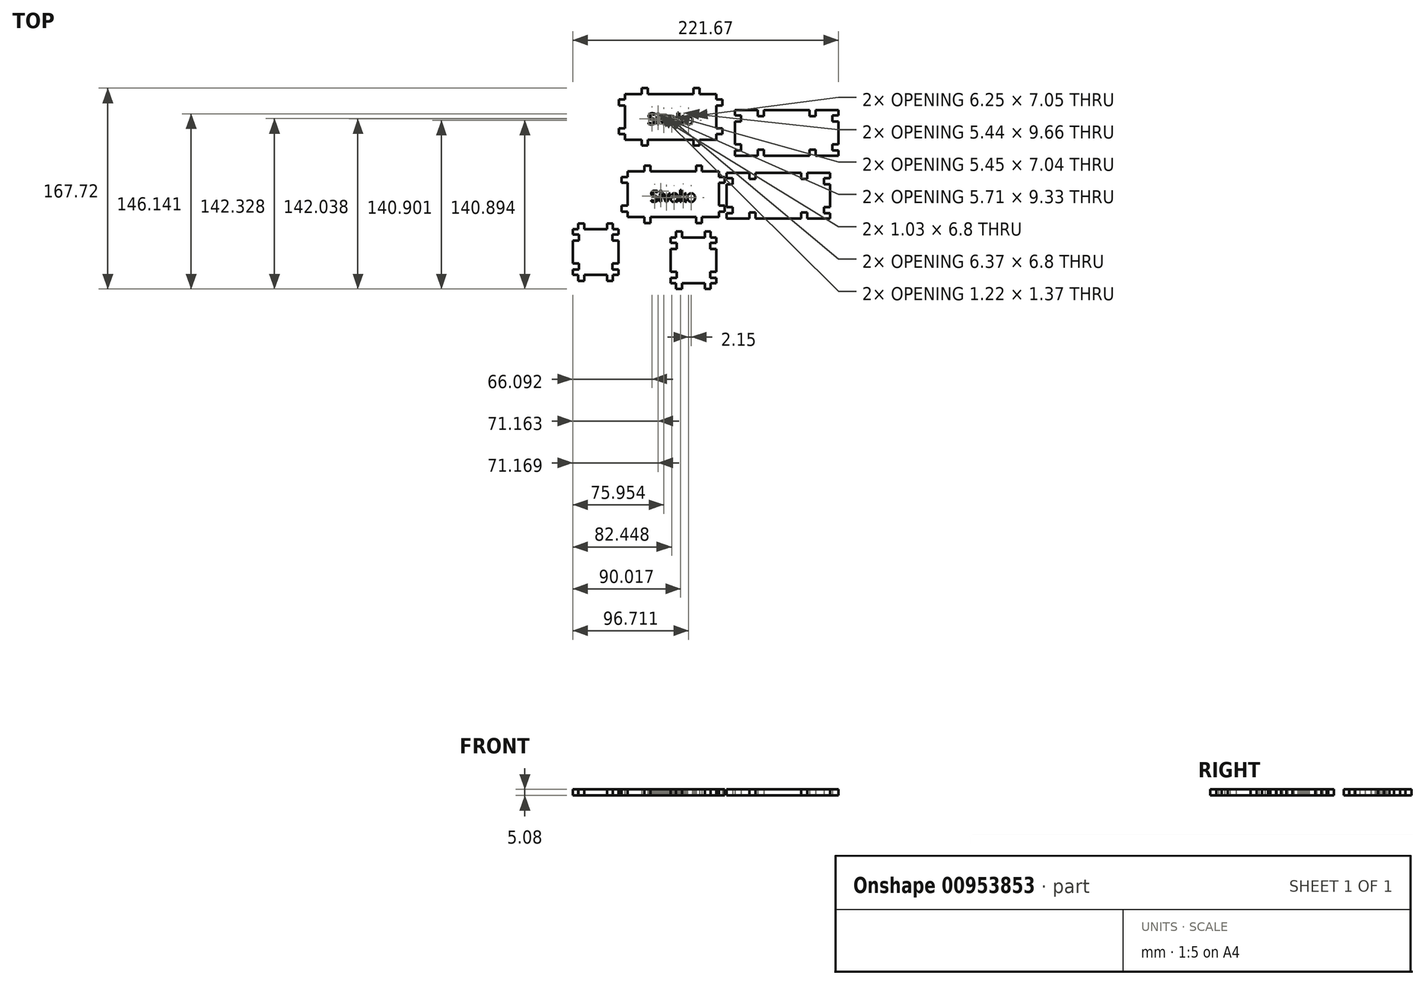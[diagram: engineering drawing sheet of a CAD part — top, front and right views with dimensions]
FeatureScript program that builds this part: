
annotation { "Feature Type Name" : "Feature", "Feature Type Description" : "" }
export const myFeature = defineFeature(function(context is Context, id is Id, definition is map)
    precondition{}
    {
        {
            var Q0;
            Q0=qCreatedBy(makeId("Top.planeOp"),FACE);
            var sketch = newSketch(context, id + "F0", { "sketchPlane" : qUnion([Q0])});
            skLineSegment(sketch, "E0.top", {"start": v(-38.1, -19.05) * mm, "end": v(38.1, -19.05) * mm});
            skLineSegment(sketch, "E0.right", {"start": v(38.1, 19.05) * mm, "end": v(38.1, -19.05) * mm});
            skPoint(sketch, "E0.middle", {"position": v(0, 0) * mm});
            skLineSegment(sketch, "E1", {"start": v(-38.1, 19.05) * mm, "end": v(-38.1, 0) * mm});
            skLineSegment(sketch, "E2", {"start": v(-38.1, 0) * mm, "end": v(-38.1, -19.05) * mm});
            skLineSegment(sketch, "E3", {"start": v(0, 0) * mm, "end": v(0, 19.05) * mm});
            skLineSegment(sketch, "E4", {"start": v(-38.1, 19.05) * mm, "end": v(0, 19.05) * mm});
            skLineSegment(sketch, "E5", {"start": v(0, 19.05) * mm, "end": v(38.1, 19.05) * mm});
            skLineSegment(sketch, "E6", {"start": v(-38.1, 0) * mm, "end": v(38.1, 0) * mm});
            skLineSegment(sketch, "E7", {"start": v(38.1, 14.61) * mm, "end": v(38.1, 14.61) * mm});
            skLineSegment(sketch, "E8", {"start": v(38.1, 9.52) * mm, "end": v(38.1, 9.52) * mm});
            skLineSegment(sketch, "E9.MirrorCS", {"start": v(38.1, -19.05) * mm, "end": v(38.1, 19.05) * mm});
            skLineSegment(sketch, "E10", {"start": v(38.1, -9.52) * mm, "end": v(38.1, -9.52) * mm});
            skLineSegment(sketch, "E11", {"start": v(38.1, -14.61) * mm, "end": v(38.1, -14.61) * mm});
            skLineSegment(sketch, "E12", {"start": v(-38.1, -14.61) * mm, "end": v(-38.1, -14.61) * mm});
            skLineSegment(sketch, "E13", {"start": v(-38.1, -9.52) * mm, "end": v(-38.1, -9.52) * mm});
            skLineSegment(sketch, "E14", {"start": v(-38.23, 9.65) * mm, "end": v(-38.23, 9.65) * mm});
            skLineSegment(sketch, "E15", {"start": v(-38.1, 9.53) * mm, "end": v(-43.05, 9.53) * mm});
            skLineSegment(sketch, "E16", {"start": v(-43.05, 9.53) * mm, "end": v(-43.05, 14.48) * mm});
            skLineSegment(sketch, "E17", {"start": v(-43.05, 14.48) * mm, "end": v(-38.1, 14.48) * mm});
            skLineSegment(sketch, "E18.MirrorCS", {"start": v(-38.1, -9.52) * mm, "end": v(-43.05, -9.52) * mm});
            skLineSegment(sketch, "E19.MirrorCS", {"start": v(-43.05, -9.52) * mm, "end": v(-43.05, -14.47) * mm});
            skLineSegment(sketch, "E20.MirrorCS", {"start": v(-43.05, -14.47) * mm, "end": v(-38.1, -14.47) * mm});
            skLineSegment(sketch, "E21", {"start": v(-38.1, -14.47) * mm, "end": v(-38.1, -14.47) * mm});
            skLineSegment(sketch, "E22.MirrorCS", {"start": v(43.05, 9.52) * mm, "end": v(43.05, 14.48) * mm});
            skLineSegment(sketch, "E23.MirrorCS", {"start": v(43.05, 14.48) * mm, "end": v(38.1, 14.48) * mm});
            skLineSegment(sketch, "E24.MirrorCS", {"start": v(38.1, 9.52) * mm, "end": v(43.05, 9.52) * mm});
            skLineSegment(sketch, "E25.MirrorCS", {"start": v(38.1, -9.52) * mm, "end": v(43.05, -9.52) * mm});
            skLineSegment(sketch, "E26.MirrorCS", {"start": v(43.05, -14.48) * mm, "end": v(38.1, -14.48) * mm});
            skLineSegment(sketch, "E27.MirrorCS", {"start": v(43.05, -9.52) * mm, "end": v(43.05, -14.48) * mm});
            skLineSegment(sketch, "E28", {"start": v(-19.05, 19.05) * mm, "end": v(-19.05, 24) * mm});
            skLineSegment(sketch, "E29", {"start": v(-19.05, 24) * mm, "end": v(-24, 24) * mm});
            skLineSegment(sketch, "E30", {"start": v(-24, 24) * mm, "end": v(-24, 19.05) * mm});
            skLineSegment(sketch, "E31.MirrorCS", {"start": v(19.05, 19.05) * mm, "end": v(19.05, 24) * mm});
            skLineSegment(sketch, "E32.MirrorCS", {"start": v(19.05, 24) * mm, "end": v(24, 24) * mm});
            skLineSegment(sketch, "E33.MirrorCS", {"start": v(24, 24) * mm, "end": v(24, 19.05) * mm});
            skLineSegment(sketch, "E34.MirrorCS", {"start": v(-19.05, -19.05) * mm, "end": v(-19.05, -24) * mm});
            skLineSegment(sketch, "E35.MirrorCS", {"start": v(-24, -24) * mm, "end": v(-24, -19.05) * mm});
            skLineSegment(sketch, "E36.MirrorCS", {"start": v(-19.05, -24) * mm, "end": v(-24, -24) * mm});
            skLineSegment(sketch, "E37.MirrorCS", {"start": v(19.05, -19.05) * mm, "end": v(19.05, -24) * mm});
            skLineSegment(sketch, "E38.MirrorCS", {"start": v(19.05, -24) * mm, "end": v(24, -24) * mm});
            skLineSegment(sketch, "E39.MirrorCS", {"start": v(24, -24) * mm, "end": v(24, -19.05) * mm});
            skLineSegment(sketch, "E40", {"start": v(0, 9.52) * mm, "end": v(-38.1, 9.53) * mm});
            skLineSegment(sketch, "E41", {"start": v(0, 0) * mm, "end": v(0, -19.05) * mm});
            skLineSegment(sketch, "E42", {"start": v(0, -9.52) * mm, "end": v(38.1, -9.52) * mm});
            skText(sketch, "E43", { "text": "Sivako", "fontName": "OpenSans-Regular.ttf"});
            skPoint(sketch, "E43.firstSnap0", {"position": v(-19.05, 9.53) * mm});
            skPoint(sketch, "E43.secondSnap0", {"position": v(19.05, -9.52) * mm});
            skLineSegment(sketch, "E44.top", {"start": v(-40.26, 45.52) * mm, "end": v(35.94, 45.52) * mm});
            skLineSegment(sketch, "E44.right", {"start": v(35.95, 83.62) * mm, "end": v(35.94, 45.52) * mm});
            skPoint(sketch, "E44.middle", {"position": v(-2.16, 64.57) * mm});
            skLineSegment(sketch, "E45", {"start": v(-40.25, 83.62) * mm, "end": v(-40.26, 64.57) * mm});
            skLineSegment(sketch, "E46", {"start": v(-40.26, 64.57) * mm, "end": v(-40.26, 45.52) * mm});
            skLineSegment(sketch, "E47", {"start": v(-2.16, 64.57) * mm, "end": v(-2.15, 83.62) * mm});
            skLineSegment(sketch, "E48", {"start": v(-40.25, 83.62) * mm, "end": v(-2.15, 83.62) * mm});
            skLineSegment(sketch, "E49", {"start": v(-2.15, 83.62) * mm, "end": v(35.95, 83.62) * mm});
            skLineSegment(sketch, "E50", {"start": v(-40.26, 64.57) * mm, "end": v(35.94, 64.57) * mm});
            skLineSegment(sketch, "E51", {"start": v(35.95, 79.18) * mm, "end": v(35.94, 79.18) * mm});
            skLineSegment(sketch, "E52", {"start": v(35.95, 74.1) * mm, "end": v(35.94, 74.1) * mm});
            skLineSegment(sketch, "E53.MirrorCS", {"start": v(35.94, 45.52) * mm, "end": v(35.95, 83.62) * mm});
            skLineSegment(sketch, "E54", {"start": v(35.94, 55.04) * mm, "end": v(35.94, 55.04) * mm});
            skLineSegment(sketch, "E55", {"start": v(35.94, 49.95) * mm, "end": v(35.94, 49.95) * mm});
            skLineSegment(sketch, "E56", {"start": v(-40.26, 49.96) * mm, "end": v(-40.26, 49.96) * mm});
            skLineSegment(sketch, "E57", {"start": v(-40.26, 55.05) * mm, "end": v(-40.26, 55.05) * mm});
            skLineSegment(sketch, "E58", {"start": v(-40.38, 74.22) * mm, "end": v(-40.38, 74.22) * mm});
            skLineSegment(sketch, "E59", {"start": v(-40.26, 74.1) * mm, "end": v(-45.2, 74.1) * mm});
            skLineSegment(sketch, "E60", {"start": v(-45.2, 74.1) * mm, "end": v(-45.2, 79.05) * mm});
            skLineSegment(sketch, "E61", {"start": v(-45.2, 79.05) * mm, "end": v(-40.26, 79.05) * mm});
            skLineSegment(sketch, "E62.MirrorCS", {"start": v(-40.26, 55.05) * mm, "end": v(-45.2, 55.05) * mm});
            skLineSegment(sketch, "E63.MirrorCS", {"start": v(-45.2, 55.05) * mm, "end": v(-45.2, 50.1) * mm});
            skLineSegment(sketch, "E64.MirrorCS", {"start": v(-45.2, 50.1) * mm, "end": v(-40.26, 50.1) * mm});
            skLineSegment(sketch, "E65", {"start": v(-40.26, 50.1) * mm, "end": v(-40.26, 50.1) * mm});
            skLineSegment(sketch, "E66", {"start": v(-40.26, 55.05) * mm, "end": v(-40.25, 55.05) * mm});
            skLineSegment(sketch, "E67.MirrorCS", {"start": v(40.9, 74.1) * mm, "end": v(40.9, 79.04) * mm});
            skLineSegment(sketch, "E68.MirrorCS", {"start": v(40.9, 79.04) * mm, "end": v(35.95, 79.04) * mm});
            skLineSegment(sketch, "E69.MirrorCS", {"start": v(35.95, 74.1) * mm, "end": v(40.9, 74.1) * mm});
            skLineSegment(sketch, "E70.MirrorCS", {"start": v(35.94, 55.04) * mm, "end": v(40.9, 55.04) * mm});
            skLineSegment(sketch, "E71.MirrorCS", {"start": v(40.9, 50.1) * mm, "end": v(35.94, 50.1) * mm});
            skLineSegment(sketch, "E72.MirrorCS", {"start": v(40.9, 55.04) * mm, "end": v(40.9, 50.1) * mm});
            skLineSegment(sketch, "E73", {"start": v(-21.2, 83.62) * mm, "end": v(-21.2, 88.57) * mm});
            skLineSegment(sketch, "E74", {"start": v(-21.2, 88.57) * mm, "end": v(-26.16, 88.57) * mm});
            skLineSegment(sketch, "E75", {"start": v(-26.16, 88.57) * mm, "end": v(-26.16, 83.62) * mm});
            skLineSegment(sketch, "E76.MirrorCS", {"start": v(16.9, 83.62) * mm, "end": v(16.9, 88.57) * mm});
            skLineSegment(sketch, "E77.MirrorCS", {"start": v(16.9, 88.57) * mm, "end": v(21.85, 88.57) * mm});
            skLineSegment(sketch, "E78.MirrorCS", {"start": v(21.85, 88.57) * mm, "end": v(21.85, 83.62) * mm});
            skLineSegment(sketch, "E79.MirrorCS", {"start": v(-21.2, 45.52) * mm, "end": v(-21.2, 40.57) * mm});
            skLineSegment(sketch, "E80.MirrorCS", {"start": v(-26.16, 40.57) * mm, "end": v(-26.16, 45.52) * mm});
            skLineSegment(sketch, "E81.MirrorCS", {"start": v(-21.2, 40.57) * mm, "end": v(-26.16, 40.57) * mm});
            skLineSegment(sketch, "E82.MirrorCS", {"start": v(16.9, 45.52) * mm, "end": v(16.9, 40.57) * mm});
            skLineSegment(sketch, "E83.MirrorCS", {"start": v(16.9, 40.57) * mm, "end": v(21.85, 40.57) * mm});
            skLineSegment(sketch, "E84.MirrorCS", {"start": v(21.85, 40.57) * mm, "end": v(21.85, 45.52) * mm});
            skLineSegment(sketch, "E85", {"start": v(-2.15, 74.1) * mm, "end": v(-40.26, 74.1) * mm});
            skLineSegment(sketch, "E86", {"start": v(-2.16, 64.57) * mm, "end": v(-2.16, 45.52) * mm});
            skLineSegment(sketch, "E87", {"start": v(-2.16, 55.04) * mm, "end": v(35.94, 55.04) * mm});
            skText(sketch, "E88", { "text": "Sivako", "fontName": "OpenSans-Regular.ttf"});
            skPoint(sketch, "E88.firstSnap0", {"position": v(-21.2, 74.1) * mm});
            skPoint(sketch, "E88.secondSnap0", {"position": v(16.9, 55.04) * mm});
            const initialGuessF0  = {"E43": [-0.01905, -0.00622, 1, 0, 0.00915], "E88": [-0.0212, 0.05835, 1, 0, 0.00915]};
            skSetInitialGuess(sketch, initialGuessF0);
            skSolve(sketch);
        }
        {
            var Q0;
            Q0 = qSketchRegion(id + "F0", true);
            var Q1;
            {var subQ6=sQuery(id+"F0.wireOp",EDGE,"E0.top");Q1=makeQuery(id+"F0.imprint","IMPRINT",FACE,{"disambiguationData":[TD([[makeQuery(id+"F0.imprint","IMPRINT",EDGE,{"derivedFrom":subQ6}),1.0]])]});}
            var Q2;
            {var subQ0=sQuery(id+"F0.wireOp",EDGE,"E43.sketch_text.stroke-40");Q2=makeQuery(id+"F0.imprint","IMPRINT",FACE,{"disambiguationData":[TD([[makeQuery(id+"F0.imprint","IMPRINT",EDGE,{"derivedFrom":subQ0}),1.0]])]});}
            var Q3;
            {var subQ0=sQuery(id+"F0.wireOp",EDGE,"E43.sketch_text.stroke-54");Q3=makeQuery(id+"F0.imprint","IMPRINT",FACE,{"disambiguationData":[TD([[makeQuery(id+"F0.imprint","IMPRINT",EDGE,{"derivedFrom":subQ0}),1.0]])]});}
            extrude(context, id + "F1", {"entities" : qUnion([Q0, Q1, Q2, Q3]), "depth" : 5.08 * mm, "offsetDistance" : 25.4 * mm});
        }
        {
            var Q0;
            Q0=qCreatedBy(makeId("Top.planeOp"),FACE);
            var sketch = newSketch(context, id + "F2", { "sketchPlane" : qUnion([Q0])});
            skLineSegment(sketch, "E89.top", {"start": v(-83.78, -67.33) * mm, "end": v(-45.68, -67.33) * mm});
            skLineSegment(sketch, "E89.right", {"start": v(-45.68, -29.23) * mm, "end": v(-45.68, -67.33) * mm});
            skPoint(sketch, "E89.middle", {"position": v(-64.73, -48.28) * mm});
            skLineSegment(sketch, "E90", {"start": v(-83.78, -48.28) * mm, "end": v(-45.68, -48.28) * mm});
            skLineSegment(sketch, "E91", {"start": v(-64.73, -29.23) * mm, "end": v(-64.73, -67.33) * mm});
            skLineSegment(sketch, "E92", {"start": v(-83.78, -29.23) * mm, "end": v(-83.78, -48.28) * mm});
            skLineSegment(sketch, "E93", {"start": v(-83.78, -48.28) * mm, "end": v(-83.78, -67.33) * mm});
            skLineSegment(sketch, "E94", {"start": v(-83.78, -38.75) * mm, "end": v(-78.7, -38.75) * mm});
            skLineSegment(sketch, "E95", {"start": v(-78.7, -38.75) * mm, "end": v(-78.7, -33.67) * mm});
            skLineSegment(sketch, "E96", {"start": v(-78.7, -33.67) * mm, "end": v(-83.78, -33.67) * mm});
            skLineSegment(sketch, "E97.MirrorCS", {"start": v(-83.78, -57.8) * mm, "end": v(-78.7, -57.8) * mm});
            skLineSegment(sketch, "E98.MirrorCS", {"start": v(-78.7, -57.8) * mm, "end": v(-78.7, -62.88) * mm});
            skLineSegment(sketch, "E99.MirrorCS", {"start": v(-78.7, -62.88) * mm, "end": v(-83.78, -62.88) * mm});
            skLineSegment(sketch, "E100.MirrorCS", {"start": v(-50.76, -38.75) * mm, "end": v(-50.76, -33.67) * mm});
            skLineSegment(sketch, "E101.MirrorCS", {"start": v(-50.76, -33.67) * mm, "end": v(-45.68, -33.67) * mm});
            skLineSegment(sketch, "E102.MirrorCS", {"start": v(-45.68, -38.75) * mm, "end": v(-50.76, -38.75) * mm});
            skLineSegment(sketch, "E103.MirrorCS", {"start": v(-45.68, -57.8) * mm, "end": v(-50.76, -57.8) * mm});
            skLineSegment(sketch, "E104.MirrorCS", {"start": v(-50.76, -57.8) * mm, "end": v(-50.76, -62.88) * mm});
            skLineSegment(sketch, "E105.MirrorCS", {"start": v(-50.76, -62.88) * mm, "end": v(-45.68, -62.88) * mm});
            skLineSegment(sketch, "E106", {"start": v(-83.78, -29.23) * mm, "end": v(-64.73, -29.23) * mm});
            skLineSegment(sketch, "E107", {"start": v(-64.73, -29.23) * mm, "end": v(-45.68, -29.23) * mm});
            skLineSegment(sketch, "E108", {"start": v(-74.25, -29.23) * mm, "end": v(-74.25, -24.28) * mm});
            skLineSegment(sketch, "E109", {"start": v(-74.25, -24.28) * mm, "end": v(-79.2, -24.28) * mm});
            skLineSegment(sketch, "E110", {"start": v(-79.2, -24.28) * mm, "end": v(-79.2, -29.23) * mm});
            skLineSegment(sketch, "E111", {"start": v(-55.2, -29.23) * mm, "end": v(-55.2, -24.28) * mm});
            skLineSegment(sketch, "E112", {"start": v(-55.2, -24.28) * mm, "end": v(-50.25, -24.28) * mm});
            skLineSegment(sketch, "E113", {"start": v(-50.25, -24.28) * mm, "end": v(-50.25, -29.23) * mm});
            skLineSegment(sketch, "E114.MirrorCS", {"start": v(-74.25, -67.33) * mm, "end": v(-74.25, -72.28) * mm});
            skLineSegment(sketch, "E115.MirrorCS", {"start": v(-74.25, -72.28) * mm, "end": v(-79.2, -72.28) * mm});
            skLineSegment(sketch, "E116.MirrorCS", {"start": v(-79.2, -72.28) * mm, "end": v(-79.2, -67.33) * mm});
            skLineSegment(sketch, "E117.MirrorCS", {"start": v(-55.2, -67.33) * mm, "end": v(-55.2, -72.28) * mm});
            skLineSegment(sketch, "E118.MirrorCS", {"start": v(-55.2, -72.28) * mm, "end": v(-50.25, -72.28) * mm});
            skLineSegment(sketch, "E119.MirrorCS", {"start": v(-50.25, -72.28) * mm, "end": v(-50.25, -67.33) * mm});
            skLineSegment(sketch, "E120.top", {"start": v(-2.2, -74.2) * mm, "end": v(35.9, -74.2) * mm});
            skLineSegment(sketch, "E120.right", {"start": v(35.9, -36.1) * mm, "end": v(35.9, -74.2) * mm});
            skPoint(sketch, "E120.middle", {"position": v(16.85, -55.15) * mm});
            skLineSegment(sketch, "E121", {"start": v(-2.2, -55.15) * mm, "end": v(35.9, -55.15) * mm});
            skLineSegment(sketch, "E122", {"start": v(16.85, -36.1) * mm, "end": v(16.85, -74.2) * mm});
            skLineSegment(sketch, "E123", {"start": v(-2.2, -36.1) * mm, "end": v(-2.2, -55.15) * mm});
            skLineSegment(sketch, "E124", {"start": v(-2.2, -55.15) * mm, "end": v(-2.2, -74.2) * mm});
            skLineSegment(sketch, "E125", {"start": v(-2.2, -45.62) * mm, "end": v(2.88, -45.62) * mm});
            skLineSegment(sketch, "E126", {"start": v(2.88, -45.62) * mm, "end": v(2.88, -40.54) * mm});
            skLineSegment(sketch, "E127", {"start": v(2.88, -40.54) * mm, "end": v(-2.2, -40.54) * mm});
            skLineSegment(sketch, "E128.MirrorCS", {"start": v(-2.2, -64.67) * mm, "end": v(2.88, -64.67) * mm});
            skLineSegment(sketch, "E129.MirrorCS", {"start": v(2.88, -64.67) * mm, "end": v(2.88, -69.75) * mm});
            skLineSegment(sketch, "E130.MirrorCS", {"start": v(2.88, -69.75) * mm, "end": v(-2.2, -69.75) * mm});
            skLineSegment(sketch, "E131.MirrorCS", {"start": v(30.82, -45.62) * mm, "end": v(30.82, -40.54) * mm});
            skLineSegment(sketch, "E132.MirrorCS", {"start": v(30.82, -40.54) * mm, "end": v(35.9, -40.54) * mm});
            skLineSegment(sketch, "E133.MirrorCS", {"start": v(35.9, -45.62) * mm, "end": v(30.82, -45.62) * mm});
            skLineSegment(sketch, "E134.MirrorCS", {"start": v(35.9, -64.67) * mm, "end": v(30.82, -64.67) * mm});
            skLineSegment(sketch, "E135.MirrorCS", {"start": v(30.82, -64.67) * mm, "end": v(30.82, -69.75) * mm});
            skLineSegment(sketch, "E136.MirrorCS", {"start": v(30.82, -69.75) * mm, "end": v(35.9, -69.75) * mm});
            skLineSegment(sketch, "E137", {"start": v(-2.2, -36.1) * mm, "end": v(16.85, -36.1) * mm});
            skLineSegment(sketch, "E138", {"start": v(16.85, -36.1) * mm, "end": v(35.9, -36.1) * mm});
            skLineSegment(sketch, "E139", {"start": v(7.33, -36.1) * mm, "end": v(7.33, -31.14) * mm});
            skLineSegment(sketch, "E140", {"start": v(7.33, -31.14) * mm, "end": v(2.37, -31.14) * mm});
            skLineSegment(sketch, "E141", {"start": v(2.37, -31.14) * mm, "end": v(2.37, -36.1) * mm});
            skLineSegment(sketch, "E142", {"start": v(26.38, -36.1) * mm, "end": v(26.38, -31.14) * mm});
            skLineSegment(sketch, "E143", {"start": v(26.38, -31.14) * mm, "end": v(31.33, -31.14) * mm});
            skLineSegment(sketch, "E144", {"start": v(31.33, -31.14) * mm, "end": v(31.33, -36.1) * mm});
            skLineSegment(sketch, "E145.MirrorCS", {"start": v(7.33, -74.2) * mm, "end": v(7.33, -79.15) * mm});
            skLineSegment(sketch, "E146.MirrorCS", {"start": v(7.33, -79.15) * mm, "end": v(2.37, -79.15) * mm});
            skLineSegment(sketch, "E147.MirrorCS", {"start": v(2.37, -79.15) * mm, "end": v(2.37, -74.2) * mm});
            skLineSegment(sketch, "E148.MirrorCS", {"start": v(26.38, -74.2) * mm, "end": v(26.38, -79.15) * mm});
            skLineSegment(sketch, "E149.MirrorCS", {"start": v(26.38, -79.15) * mm, "end": v(31.33, -79.15) * mm});
            skLineSegment(sketch, "E150.MirrorCS", {"start": v(31.33, -79.15) * mm, "end": v(31.33, -74.2) * mm});
            skLineSegment(sketch, "E151.top", {"start": v(44.41, -20.23) * mm, "end": v(130.77, -20.23) * mm});
            skLineSegment(sketch, "E151.right", {"start": v(130.77, 17.87) * mm, "end": v(130.77, -20.23) * mm});
            skPoint(sketch, "E151.middle", {"position": v(87.6, -1.18) * mm});
            skLineSegment(sketch, "E152", {"start": v(44.41, 17.87) * mm, "end": v(44.41, -1.18) * mm});
            skLineSegment(sketch, "E153", {"start": v(44.41, -1.18) * mm, "end": v(44.41, -20.23) * mm});
            skLineSegment(sketch, "E154", {"start": v(44.41, 17.87) * mm, "end": v(87.6, 17.87) * mm});
            skLineSegment(sketch, "E155", {"start": v(87.6, 17.87) * mm, "end": v(130.77, 17.87) * mm});
            skLineSegment(sketch, "E156", {"start": v(87.6, 17.87) * mm, "end": v(49.5, 17.87) * mm});
            skLineSegment(sketch, "E157", {"start": v(87.6, 17.87) * mm, "end": v(125.7, 17.87) * mm});
            skLineSegment(sketch, "E158", {"start": v(68.54, 17.87) * mm, "end": v(68.54, 12.8) * mm});
            skLineSegment(sketch, "E159", {"start": v(68.54, 12.8) * mm, "end": v(63.46, 12.8) * mm});
            skLineSegment(sketch, "E160", {"start": v(63.46, 12.8) * mm, "end": v(63.46, 17.87) * mm});
            skLineSegment(sketch, "E161.MirrorCS", {"start": v(106.64, 17.87) * mm, "end": v(106.64, 12.8) * mm});
            skLineSegment(sketch, "E162.MirrorCS", {"start": v(106.64, 12.8) * mm, "end": v(111.72, 12.8) * mm});
            skLineSegment(sketch, "E163.MirrorCS", {"start": v(111.72, 12.8) * mm, "end": v(111.72, 17.87) * mm});
            skLineSegment(sketch, "E164.MirrorCS", {"start": v(68.54, -15.15) * mm, "end": v(63.46, -15.15) * mm});
            skLineSegment(sketch, "E165.MirrorCS", {"start": v(63.46, -15.15) * mm, "end": v(63.46, -20.23) * mm});
            skLineSegment(sketch, "E166.MirrorCS", {"start": v(68.54, -20.23) * mm, "end": v(68.54, -15.15) * mm});
            skLineSegment(sketch, "E167.MirrorCS", {"start": v(106.64, -15.15) * mm, "end": v(111.72, -15.15) * mm});
            skLineSegment(sketch, "E168.MirrorCS", {"start": v(106.64, -20.23) * mm, "end": v(106.64, -15.15) * mm});
            skLineSegment(sketch, "E169.MirrorCS", {"start": v(111.72, -15.15) * mm, "end": v(111.72, -20.23) * mm});
            skLineSegment(sketch, "E170.MirrorCS", {"start": v(49.5, 13.43) * mm, "end": v(44.41, 13.43) * mm});
            skLineSegment(sketch, "E171.MirrorCS", {"start": v(49.5, 8.35) * mm, "end": v(49.5, 13.43) * mm});
            skLineSegment(sketch, "E172.MirrorCS", {"start": v(44.41, 8.35) * mm, "end": v(49.5, 8.35) * mm});
            skLineSegment(sketch, "E173.MirrorCS", {"start": v(49.5, -10.7) * mm, "end": v(49.5, -15.78) * mm});
            skLineSegment(sketch, "E174.MirrorCS", {"start": v(49.5, -15.78) * mm, "end": v(44.41, -15.78) * mm});
            skLineSegment(sketch, "E175.MirrorCS", {"start": v(44.41, -10.7) * mm, "end": v(49.5, -10.7) * mm});
            skLineSegment(sketch, "E176.MirrorCS", {"start": v(125.7, 8.35) * mm, "end": v(125.7, 13.43) * mm});
            skLineSegment(sketch, "E177.MirrorCS", {"start": v(125.7, 13.43) * mm, "end": v(130.77, 13.43) * mm});
            skLineSegment(sketch, "E178.MirrorCS", {"start": v(130.77, 8.35) * mm, "end": v(125.7, 8.35) * mm});
            skLineSegment(sketch, "E179.MirrorCS", {"start": v(130.77, -10.7) * mm, "end": v(125.7, -10.7) * mm});
            skLineSegment(sketch, "E180.MirrorCS", {"start": v(125.7, -10.7) * mm, "end": v(125.7, -15.78) * mm});
            skLineSegment(sketch, "E181.MirrorCS", {"start": v(125.7, -15.78) * mm, "end": v(130.77, -15.78) * mm});
            skLineSegment(sketch, "E182.top", {"start": v(51.53, 32.1) * mm, "end": v(137.89, 32.1) * mm});
            skLineSegment(sketch, "E182.right", {"start": v(137.89, 70.2) * mm, "end": v(137.89, 32.1) * mm});
            skPoint(sketch, "E182.middle", {"position": v(94.7, 51.15) * mm});
            skLineSegment(sketch, "E183", {"start": v(51.53, 51.15) * mm, "end": v(137.89, 51.15) * mm});
            skLineSegment(sketch, "E184", {"start": v(51.53, 70.2) * mm, "end": v(51.53, 51.15) * mm});
            skLineSegment(sketch, "E185", {"start": v(51.53, 51.15) * mm, "end": v(51.53, 32.1) * mm});
            skLineSegment(sketch, "E186", {"start": v(94.7, 51.15) * mm, "end": v(94.7, 70.2) * mm});
            skLineSegment(sketch, "E187", {"start": v(51.53, 70.2) * mm, "end": v(94.7, 70.2) * mm});
            skLineSegment(sketch, "E188", {"start": v(94.7, 70.2) * mm, "end": v(137.89, 70.2) * mm});
            skLineSegment(sketch, "E189", {"start": v(94.7, 70.2) * mm, "end": v(56.6, 70.2) * mm});
            skLineSegment(sketch, "E190", {"start": v(94.7, 70.2) * mm, "end": v(132.8, 70.2) * mm});
            skLineSegment(sketch, "E191", {"start": v(75.66, 70.2) * mm, "end": v(75.66, 65.12) * mm});
            skLineSegment(sketch, "E192", {"start": v(75.66, 65.12) * mm, "end": v(70.58, 65.12) * mm});
            skLineSegment(sketch, "E193", {"start": v(70.58, 65.12) * mm, "end": v(70.58, 70.2) * mm});
            skLineSegment(sketch, "E194.MirrorCS", {"start": v(113.76, 70.2) * mm, "end": v(113.76, 65.12) * mm});
            skLineSegment(sketch, "E195.MirrorCS", {"start": v(113.76, 65.12) * mm, "end": v(118.84, 65.12) * mm});
            skLineSegment(sketch, "E196.MirrorCS", {"start": v(118.84, 65.12) * mm, "end": v(118.84, 70.2) * mm});
            skLineSegment(sketch, "E197.MirrorCS", {"start": v(75.66, 37.18) * mm, "end": v(70.58, 37.18) * mm});
            skLineSegment(sketch, "E198.MirrorCS", {"start": v(70.58, 37.18) * mm, "end": v(70.58, 32.1) * mm});
            skLineSegment(sketch, "E199.MirrorCS", {"start": v(75.66, 32.1) * mm, "end": v(75.66, 37.18) * mm});
            skLineSegment(sketch, "E200.MirrorCS", {"start": v(113.76, 37.18) * mm, "end": v(118.84, 37.18) * mm});
            skLineSegment(sketch, "E201.MirrorCS", {"start": v(113.76, 32.1) * mm, "end": v(113.76, 37.18) * mm});
            skLineSegment(sketch, "E202.MirrorCS", {"start": v(118.84, 37.18) * mm, "end": v(118.84, 32.1) * mm});
            skLineSegment(sketch, "E203.MirrorCS", {"start": v(56.6, 65.76) * mm, "end": v(51.53, 65.76) * mm});
            skLineSegment(sketch, "E204.MirrorCS", {"start": v(56.6, 60.68) * mm, "end": v(56.6, 65.76) * mm});
            skLineSegment(sketch, "E205.MirrorCS", {"start": v(51.53, 60.68) * mm, "end": v(56.6, 60.68) * mm});
            skLineSegment(sketch, "E206.MirrorCS", {"start": v(56.6, 41.63) * mm, "end": v(56.6, 36.55) * mm});
            skLineSegment(sketch, "E207.MirrorCS", {"start": v(56.6, 36.55) * mm, "end": v(51.53, 36.55) * mm});
            skLineSegment(sketch, "E208.MirrorCS", {"start": v(51.53, 41.63) * mm, "end": v(56.6, 41.63) * mm});
            skLineSegment(sketch, "E209.MirrorCS", {"start": v(132.8, 60.68) * mm, "end": v(132.8, 65.76) * mm});
            skLineSegment(sketch, "E210.MirrorCS", {"start": v(132.8, 65.76) * mm, "end": v(137.89, 65.76) * mm});
            skLineSegment(sketch, "E211.MirrorCS", {"start": v(137.89, 60.68) * mm, "end": v(132.8, 60.68) * mm});
            skLineSegment(sketch, "E212.MirrorCS", {"start": v(137.89, 41.63) * mm, "end": v(132.8, 41.63) * mm});
            skLineSegment(sketch, "E213.MirrorCS", {"start": v(132.8, 41.63) * mm, "end": v(132.8, 36.55) * mm});
            skLineSegment(sketch, "E214.MirrorCS", {"start": v(132.8, 36.55) * mm, "end": v(137.89, 36.55) * mm});
            skPoint(sketch, "E215.orphan", {"position": v(130.77, -1.18) * mm});
            skSolve(sketch);
        }
        {
            var Q0;
            {var subQ0=sQuery(id+"F2.wireOp",EDGE,"E94");Q0=makeQuery(id+"F2.imprint","IMPRINT",FACE,{"disambiguationData":[TD([[makeQuery(id+"F2.imprint","IMPRINT",EDGE,{"derivedFrom":subQ0}),-1.0]])]});}
            var Q1;
            {var subQ10=sQuery(id+"F2.wireOp",EDGE,"E97.MirrorCS");Q1=makeQuery(id+"F2.imprint","IMPRINT",FACE,{"disambiguationData":[TD([[makeQuery(id+"F2.imprint","IMPRINT",EDGE,{"derivedFrom":subQ10}),1.0]])]});}
            var Q2;
            {var subQ3=sQuery(id+"F2.wireOp",EDGE,"E103.MirrorCS");Q2=makeQuery(id+"F2.imprint","IMPRINT",FACE,{"disambiguationData":[TD([[makeQuery(id+"F2.imprint","IMPRINT",EDGE,{"derivedFrom":subQ3}),-1.0]])]});}
            var Q3;
            Q3=makeQuery(id+"F2.imprint","IMPRINT",FACE,{"disambiguationData":[TD([[makeQuery(id+"F2.imprint","IMPRINT",EDGE,{"derivedFrom":sQuery(id+"F2.wireOp",EDGE,"E100.MirrorCS")}),1.0]])]});
            var Q4;
            {var subQ0=sQuery(id+"F2.wireOp",EDGE,"E117.MirrorCS");Q4=makeQuery(id+"F2.imprint","IMPRINT",FACE,{"disambiguationData":[TD([[makeQuery(id+"F2.imprint","IMPRINT",EDGE,{"derivedFrom":subQ0}),1.0]])]});}
            var Q5;
            {var subQ0=sQuery(id+"F2.wireOp",EDGE,"E114.MirrorCS");Q5=makeQuery(id+"F2.imprint","IMPRINT",FACE,{"disambiguationData":[TD([[makeQuery(id+"F2.imprint","IMPRINT",EDGE,{"derivedFrom":subQ0}),-1.0]])]});}
            var Q6;
            {var subQ0=sQuery(id+"F2.wireOp",EDGE,"E108");Q6=makeQuery(id+"F2.imprint","IMPRINT",FACE,{"disambiguationData":[TD([[makeQuery(id+"F2.imprint","IMPRINT",EDGE,{"derivedFrom":subQ0}),1.0]])]});}
            var Q7;
            {var subQ0=sQuery(id+"F2.wireOp",EDGE,"E111");Q7=makeQuery(id+"F2.imprint","IMPRINT",FACE,{"disambiguationData":[TD([[makeQuery(id+"F2.imprint","IMPRINT",EDGE,{"derivedFrom":subQ0}),-1.0]])]});}
            var Q8;
            {var subQ10=sQuery(id+"F2.wireOp",EDGE,"E128.MirrorCS");Q8=makeQuery(id+"F2.imprint","IMPRINT",FACE,{"disambiguationData":[TD([[makeQuery(id+"F2.imprint","IMPRINT",EDGE,{"derivedFrom":subQ10}),1.0]])]});}
            var Q9;
            {var subQ3=sQuery(id+"F2.wireOp",EDGE,"E134.MirrorCS");Q9=makeQuery(id+"F2.imprint","IMPRINT",FACE,{"disambiguationData":[TD([[makeQuery(id+"F2.imprint","IMPRINT",EDGE,{"derivedFrom":subQ3}),-1.0]])]});}
            var Q10;
            Q10=makeQuery(id+"F2.imprint","IMPRINT",FACE,{"disambiguationData":[TD([[makeQuery(id+"F2.imprint","IMPRINT",EDGE,{"derivedFrom":sQuery(id+"F2.wireOp",EDGE,"E131.MirrorCS")}),1.0]])]});
            var Q11;
            {var subQ0=sQuery(id+"F2.wireOp",EDGE,"E125");Q11=makeQuery(id+"F2.imprint","IMPRINT",FACE,{"disambiguationData":[TD([[makeQuery(id+"F2.imprint","IMPRINT",EDGE,{"derivedFrom":subQ0}),-1.0]])]});}
            var Q12;
            {var subQ0=sQuery(id+"F2.wireOp",EDGE,"E148.MirrorCS");Q12=makeQuery(id+"F2.imprint","IMPRINT",FACE,{"disambiguationData":[TD([[makeQuery(id+"F2.imprint","IMPRINT",EDGE,{"derivedFrom":subQ0}),1.0]])]});}
            var Q13;
            {var subQ0=sQuery(id+"F2.wireOp",EDGE,"E145.MirrorCS");Q13=makeQuery(id+"F2.imprint","IMPRINT",FACE,{"disambiguationData":[TD([[makeQuery(id+"F2.imprint","IMPRINT",EDGE,{"derivedFrom":subQ0}),-1.0]])]});}
            var Q14;
            {var subQ0=sQuery(id+"F2.wireOp",EDGE,"E139");Q14=makeQuery(id+"F2.imprint","IMPRINT",FACE,{"disambiguationData":[TD([[makeQuery(id+"F2.imprint","IMPRINT",EDGE,{"derivedFrom":subQ0}),1.0]])]});}
            var Q15;
            {var subQ0=sQuery(id+"F2.wireOp",EDGE,"E142");Q15=makeQuery(id+"F2.imprint","IMPRINT",FACE,{"disambiguationData":[TD([[makeQuery(id+"F2.imprint","IMPRINT",EDGE,{"derivedFrom":subQ0}),-1.0]])]});}
            extrude(context, id + "F3", {"entities" : qUnion([Q0, Q1, Q2, Q3, Q4, Q5, Q6, Q7, Q8, Q9, Q10, Q11, Q12, Q13, Q14, Q15]), "depth" : 5.08 * mm, "offsetDistance" : 25.4 * mm});
        }
        {
            var Q0;
            {var subQ3=sQuery(id+"F2.wireOp",EDGE,"78740de0-593b-4ee4-b9a7-870c1f821584");Q0=makeQuery(id+"F2.imprint","IMPRINT",FACE,{"disambiguationData":[TD([[makeQuery(id+"F2.imprint","IMPRINT",EDGE,{"derivedFrom":subQ3}),1.0]])]});}
            var Q1;
            {var subQ12=sQuery(id+"F2.wireOp",EDGE,"E158");Q1=makeQuery(id+"F2.imprint","IMPRINT",FACE,{"disambiguationData":[TD([[makeQuery(id+"F2.imprint","IMPRINT",EDGE,{"derivedFrom":subQ12}),1.0]])]});}
            var Q2;
            {var subQ2=sQuery(id+"F2.wireOp",EDGE,"78740de0-593b-4ee4-b9a7-870c1f821584");Q2=makeQuery(id+"F2.imprint","IMPRINT",FACE,{"disambiguationData":[TD([[makeQuery(id+"F2.imprint","IMPRINT",EDGE,{"derivedFrom":subQ2}),-1.0]])]});}
            var Q3;
            Q3=makeQuery(id+"F2.imprint","IMPRINT",FACE,{"disambiguationData":[TD([[makeQuery(id+"F2.imprint","IMPRINT",EDGE,{"derivedFrom":sQuery(id+"F2.wireOp",EDGE,"E197.MirrorCS")}),-1.0]])]});
            var Q4;
            {var subQ6=sQuery(id+"F2.wireOp",EDGE,"E186");Q4=makeQuery(id+"F2.imprint","IMPRINT",FACE,{"disambiguationData":[TD([[makeQuery(id+"F2.imprint","IMPRINT",EDGE,{"derivedFrom":subQ6}),1.0]])]});}
            var Q5;
            {var subQ8=sQuery(id+"F2.wireOp",EDGE,"E186");Q5=makeQuery(id+"F2.imprint","IMPRINT",FACE,{"disambiguationData":[TD([[makeQuery(id+"F2.imprint","IMPRINT",EDGE,{"derivedFrom":subQ8}),-1.0]])]});}
            extrude(context, id + "F4", {"entities" : qUnion([Q0, Q1, Q2, Q3, Q4, Q5]), "depth" : 5.08 * mm, "offsetDistance" : 25.4 * mm});
        }
    });
